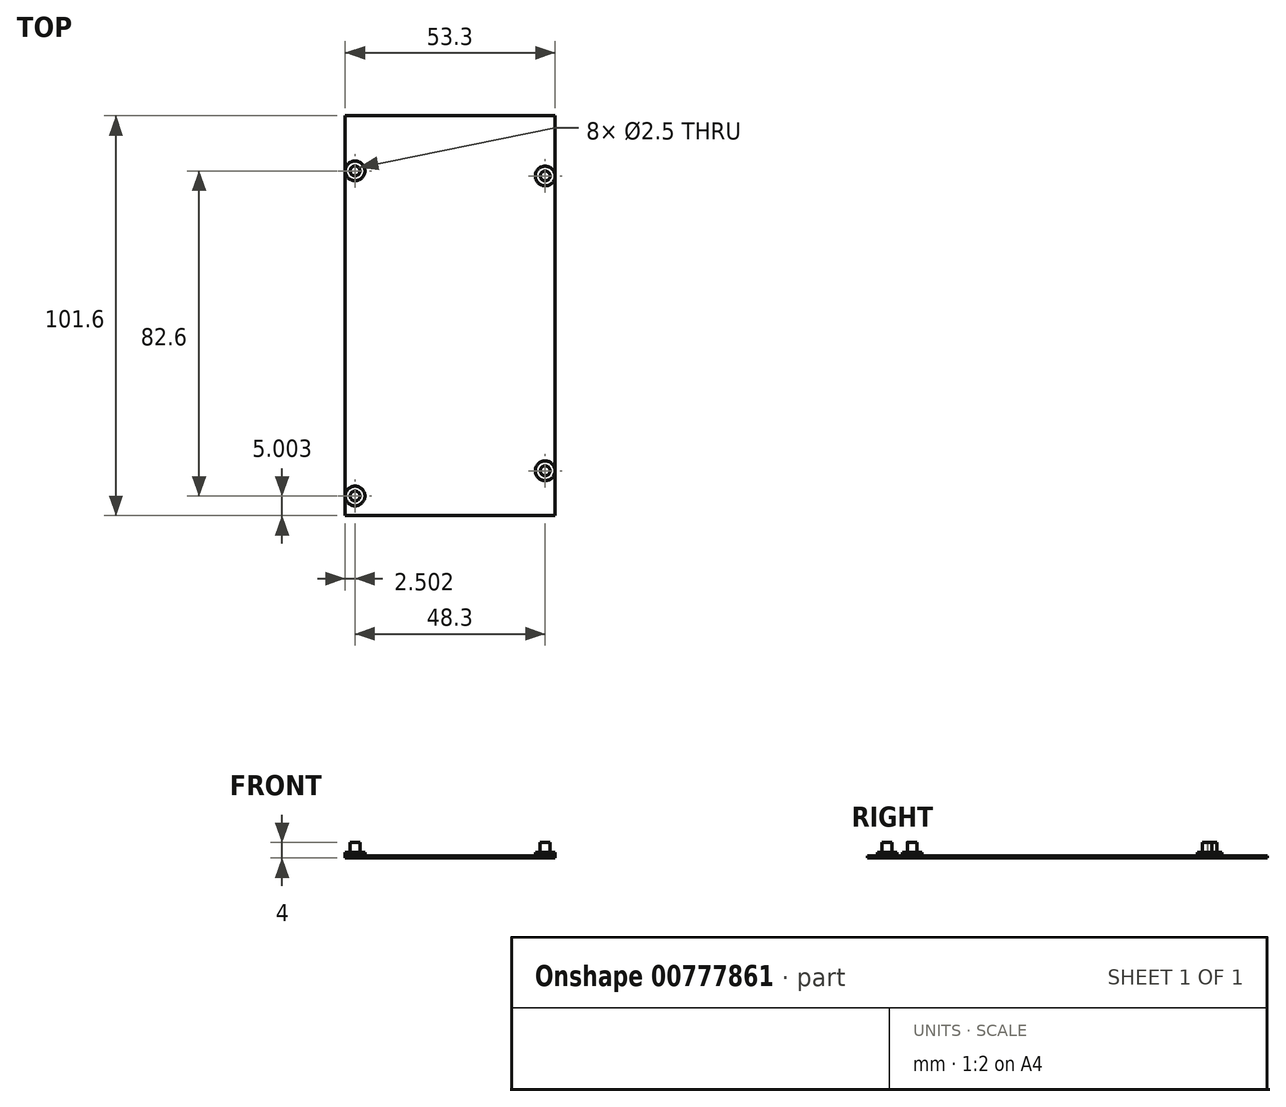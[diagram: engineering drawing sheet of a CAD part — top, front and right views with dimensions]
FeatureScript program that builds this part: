
annotation { "Feature Type Name" : "Feature", "Feature Type Description" : "" }
export const myFeature = defineFeature(function(context is Context, id is Id, definition is map)
    precondition{}
    {
        {
            var Q0;
            Q0=qCreatedBy(makeId("Top.planeOp"),FACE);
            var sketch = newSketch(context, id + "F0", { "sketchPlane" : qUnion([Q0])});
            skLineSegment(sketch, "E0.bottom", {"start": v(-22.77, 45.35) * mm, "end": v(30.53, 45.35) * mm});
            skLineSegment(sketch, "E0.top", {"start": v(-22.77, -56.25) * mm, "end": v(30.53, -56.25) * mm});
            skLineSegment(sketch, "E0.left", {"start": v(-22.77, 45.35) * mm, "end": v(-22.77, -56.25) * mm});
            skLineSegment(sketch, "E0.right", {"start": v(30.53, 45.35) * mm, "end": v(30.53, -56.25) * mm});
            skPoint(sketch, "E0.middle", {"position": v(3.88, -5.45) * mm});
            skPoint(sketch, "E0.middle.positionSnap0", {"position": v(3.88, 53.75) * mm});
            skPoint(sketch, "E0.middle.positionSnap1", {"position": v(-29.12, -5.45) * mm});
            skPoint(sketch, "E0.centerSnap0", {"position": v(3.88, 53.75) * mm});
            skPoint(sketch, "E0.centerSnap1", {"position": v(-29.12, -5.45) * mm});
            skCircle(sketch, "E1", {"center": v(-20.27, -51.25) * mm, "radius": 1.25 * mm});
            skCircle(sketch, "E2", {"center": v(28.03, -44.85) * mm, "radius": 1.25 * mm});
            skCircle(sketch, "E3", {"center": v(-20.27, 31.35) * mm, "radius": 1.25 * mm});
            skCircle(sketch, "E4", {"center": v(28.03, 30.05) * mm, "radius": 1.25 * mm});
            skCircle(sketch, "E5", {"center": v(-20.27, 31.35) * mm, "radius": 2.5 * mm});
            skCircle(sketch, "E6", {"center": v(28.03, 30.05) * mm, "radius": 2.5 * mm});
            skCircle(sketch, "E7", {"center": v(-20.27, -51.25) * mm, "radius": 2.5 * mm});
            skCircle(sketch, "E8", {"center": v(28.03, -44.85) * mm, "radius": 2.5 * mm});
            skSolve(sketch);
        }
        {
            var Q0;
            Q0=makeQuery(id+"F0.imprint","IMPRINT",FACE,{"disambiguationData":[TD([[makeQuery(id+"F0.imprint","IMPRINT",EDGE,{"derivedFrom":sQuery(id+"F0.wireOp",EDGE,"E3")}),-1.0]])]});
            var Q1;
            Q1=makeQuery(id+"F0.imprint","IMPRINT",FACE,{"disambiguationData":[TD([[makeQuery(id+"F0.imprint","IMPRINT",EDGE,{"derivedFrom":sQuery(id+"F0.wireOp",EDGE,"E4")}),-1.0]])]});
            var Q2;
            Q2=makeQuery(id+"F0.imprint","IMPRINT",FACE,{"disambiguationData":[TD([[makeQuery(id+"F0.imprint","IMPRINT",EDGE,{"derivedFrom":sQuery(id+"F0.wireOp",EDGE,"E1")}),-1.0]])]});
            var Q3;
            Q3=makeQuery(id+"F0.imprint","IMPRINT",FACE,{"disambiguationData":[TD([[makeQuery(id+"F0.imprint","IMPRINT",EDGE,{"derivedFrom":sQuery(id+"F0.wireOp",EDGE,"E2")}),-1.0]])]});
            extrude(context, id + "F1", {"entities" : qUnion([Q0, Q1, Q2, Q3]), "depth" : 1.5 * mm, "offsetDistance" : 25 * mm});
        }
        {
            var Q0;
            Q0 = qSketchRegion(id + "F0", true);
            extrude(context, id + "F2", {"entities" : qUnion([Q0]), "depth" : 0.5 * mm, "offsetDistance" : 25 * mm});
        }
        {
            var Q0;
            Q0=makeQuery(id+"F0.imprint","IMPRINT",FACE,{"disambiguationData":[TD([[makeQuery(id+"F0.imprint","IMPRINT",EDGE,{"derivedFrom":sQuery(id+"F0.wireOp",EDGE,"E3")}),1.0]])]});
            var Q1;
            Q1=makeQuery(id+"F0.imprint","IMPRINT",FACE,{"disambiguationData":[TD([[makeQuery(id+"F0.imprint","IMPRINT",EDGE,{"derivedFrom":sQuery(id+"F0.wireOp",EDGE,"E4")}),1.0]])]});
            var Q2;
            Q2=makeQuery(id+"F0.imprint","IMPRINT",FACE,{"disambiguationData":[TD([[makeQuery(id+"F0.imprint","IMPRINT",EDGE,{"derivedFrom":sQuery(id+"F0.wireOp",EDGE,"E1")}),1.0]])]});
            var Q3;
            Q3=makeQuery(id+"F0.imprint","IMPRINT",FACE,{"disambiguationData":[TD([[makeQuery(id+"F0.imprint","IMPRINT",EDGE,{"derivedFrom":sQuery(id+"F0.wireOp",EDGE,"E2")}),1.0]])]});
            extrude(context, id + "F3", {"entities" : qUnion([Q0, Q1, Q2, Q3]), "depth" : 4 * mm, "offsetDistance" : 25 * mm});
        }
    });
